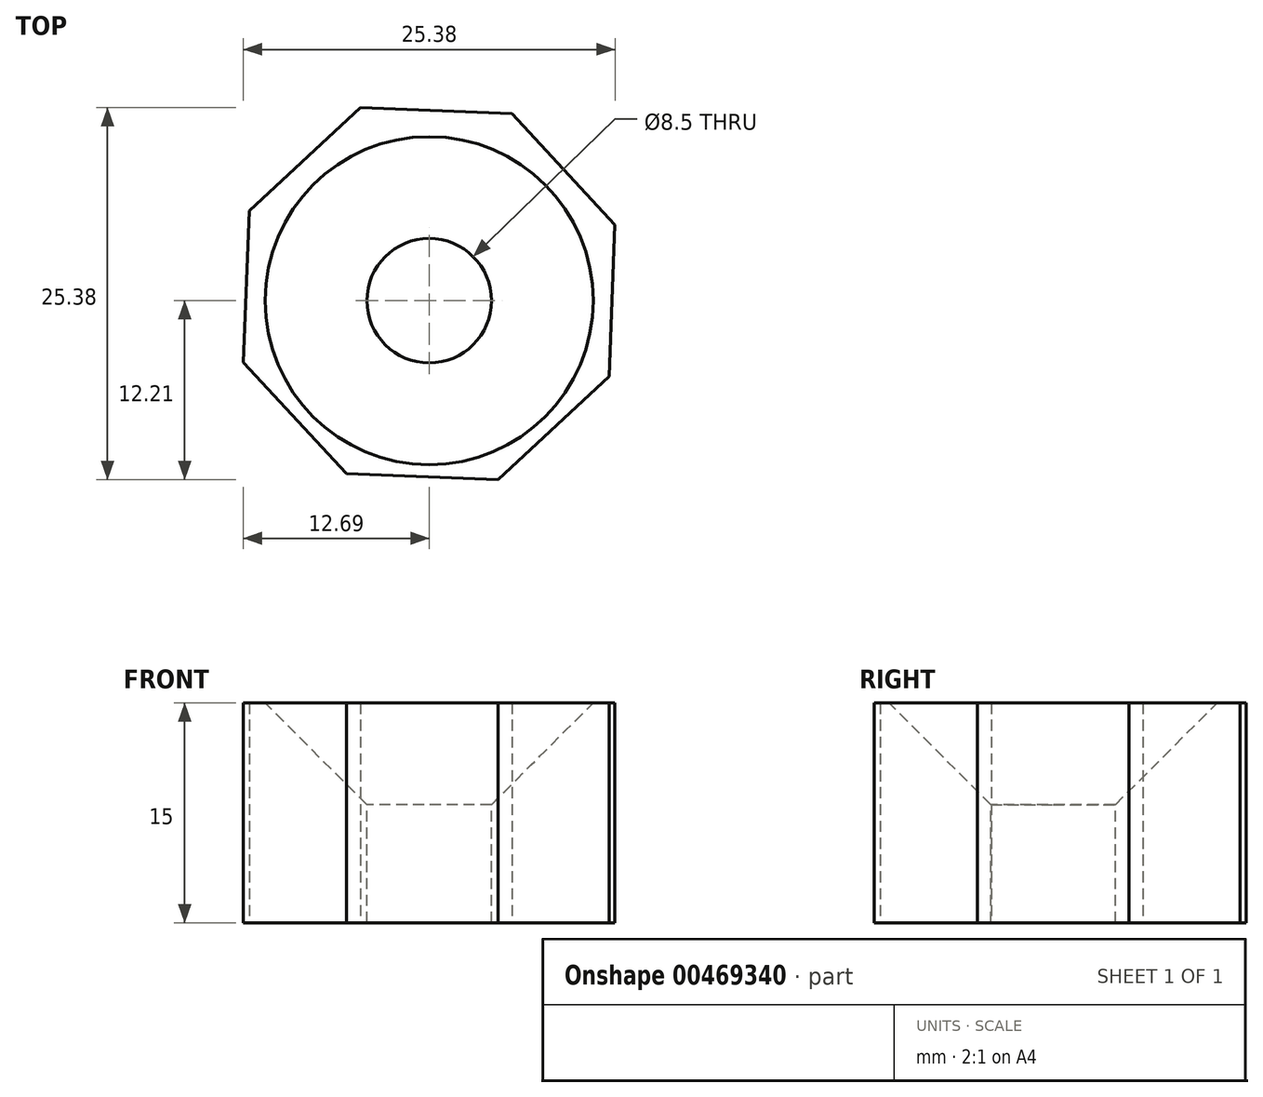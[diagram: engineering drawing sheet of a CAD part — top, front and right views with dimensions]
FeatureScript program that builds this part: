
annotation { "Feature Type Name" : "Feature", "Feature Type Description" : "" }
export const myFeature = defineFeature(function(context is Context, id is Id, definition is map)
    precondition{}
    {
        {
            var Q0;
            Q0=qCreatedBy(makeId("Top.planeOp"),FACE);
            var sketch = newSketch(context, id + "F0", { "sketchPlane" : qUnion([Q0])});
            skCircle(sketch, "E0.cCircle", {"center": v(0, 0.48) * mm, "radius": 12.5 * mm, "construction": true});
            skLineSegment(sketch, "E0.0", {"start": v(12.69, 5.17) * mm, "end": v(12.3, -5.17) * mm});
            skLineSegment(sketch, "E0.1", {"start": v(12.3, -5.17) * mm, "end": v(4.7, -12.2) * mm});
            skLineSegment(sketch, "E0.2", {"start": v(4.7, -12.2) * mm, "end": v(-5.65, -11.81) * mm});
            skLineSegment(sketch, "E0.3", {"start": v(-5.65, -11.81) * mm, "end": v(-12.69, -4.21) * mm});
            skLineSegment(sketch, "E0.4", {"start": v(-12.69, -4.21) * mm, "end": v(-12.3, 6.13) * mm});
            skLineSegment(sketch, "E0.5", {"start": v(-12.3, 6.13) * mm, "end": v(-4.7, 13.17) * mm});
            skLineSegment(sketch, "E0.6", {"start": v(-4.7, 13.17) * mm, "end": v(5.65, 12.77) * mm});
            skLineSegment(sketch, "E0.7", {"start": v(5.65, 12.77) * mm, "end": v(12.69, 5.17) * mm});
            skPoint(sketch, "E0.0.midPoint", {"position": v(12.5, 0) * mm});
            skSolve(sketch);
        }
        {
            var Q0;
            Q0=makeQuery(id+"F0.imprint","IMPRINT",FACE,{"disambiguationData":[TD([[makeQuery(id+"F0.imprint","IMPRINT",EDGE,{"derivedFrom":sQuery(id+"F0.wireOp",EDGE,"E0.0")}),-1.0]])]});
            extrude(context, id + "F1", {"entities" : qUnion([Q0]), "depth" : 15 * mm});
        }
        {
            var Q0;
            Q0=makeQuery(id+"F1.opExtrude","CAP_FACE",FACE,{"disambiguationData":[OSD([sQuery(id+"F0.wireOp",EDGE,"E0.0"),sQuery(id+"F0.wireOp",EDGE,"E0.1"),sQuery(id+"F0.wireOp",EDGE,"E0.2"),sQuery(id+"F0.wireOp",EDGE,"E0.3"),sQuery(id+"F0.wireOp",EDGE,"E0.4"),sQuery(id+"F0.wireOp",EDGE,"E0.5"),sQuery(id+"F0.wireOp",EDGE,"E0.6"),sQuery(id+"F0.wireOp",EDGE,"E0.7")])],"isStart":false});
            var sketch = newSketch(context, id + "F2", { "sketchPlane" : qUnion([Q0])});
            skCircle(sketch, "E1", {"center": v(0, 0) * mm, "radius": 3.08 * mm});
            skSolve(sketch);
        }
        {
            var Q0;
            Q0=sQuery(id+"F2.wireOp",VERTEX,"E1.center");
            var Q1;
            Q1=makeQuery(id+"F1.opExtrude","SWEPT_BODY",BODY,{"disambiguationData":[OSD([sQuery(id+"F0.wireOp",EDGE,"E0.0"),sQuery(id+"F0.wireOp",EDGE,"E0.1"),sQuery(id+"F0.wireOp",EDGE,"E0.2"),sQuery(id+"F0.wireOp",EDGE,"E0.3"),sQuery(id+"F0.wireOp",EDGE,"E0.4"),sQuery(id+"F0.wireOp",EDGE,"E0.5"),sQuery(id+"F0.wireOp",EDGE,"E0.6"),sQuery(id+"F0.wireOp",EDGE,"E0.7")])]});
            hole(context, id + "F3", {"style" : HoleStyle.C_SINK, "endStyle" : HoleEndStyle.THROUGH, "standardTappedOrClearance" : lookupTablePath({ "standard" : "ISO", "engagement" : "75%", "pitch" : "1.5 mm", "size" : "M10", "type" : "Tapped" }), "standardBlindInLast" : lookupTablePath({ "standard" : "ISO", "engagement" : "75%", "pitch" : "1.5 mm", "size" : "M10", "type" : "Tapped" }), "holeDiameter" : 8.5 * mm, "cSinkDiameter" : 22.4 * mm, "cSinkAngle" : 90 * degree, "showTappedDepth" : true, "isTappedThrough" : true, "tappedDepth" : 12 * mm, "tapClearance" : 3, "startFromSketch" : true, "locations" : qUnion([Q0]), "scope" : qUnion([Q1]), "majorDiameter" : 10 * mm});
        }
    });
